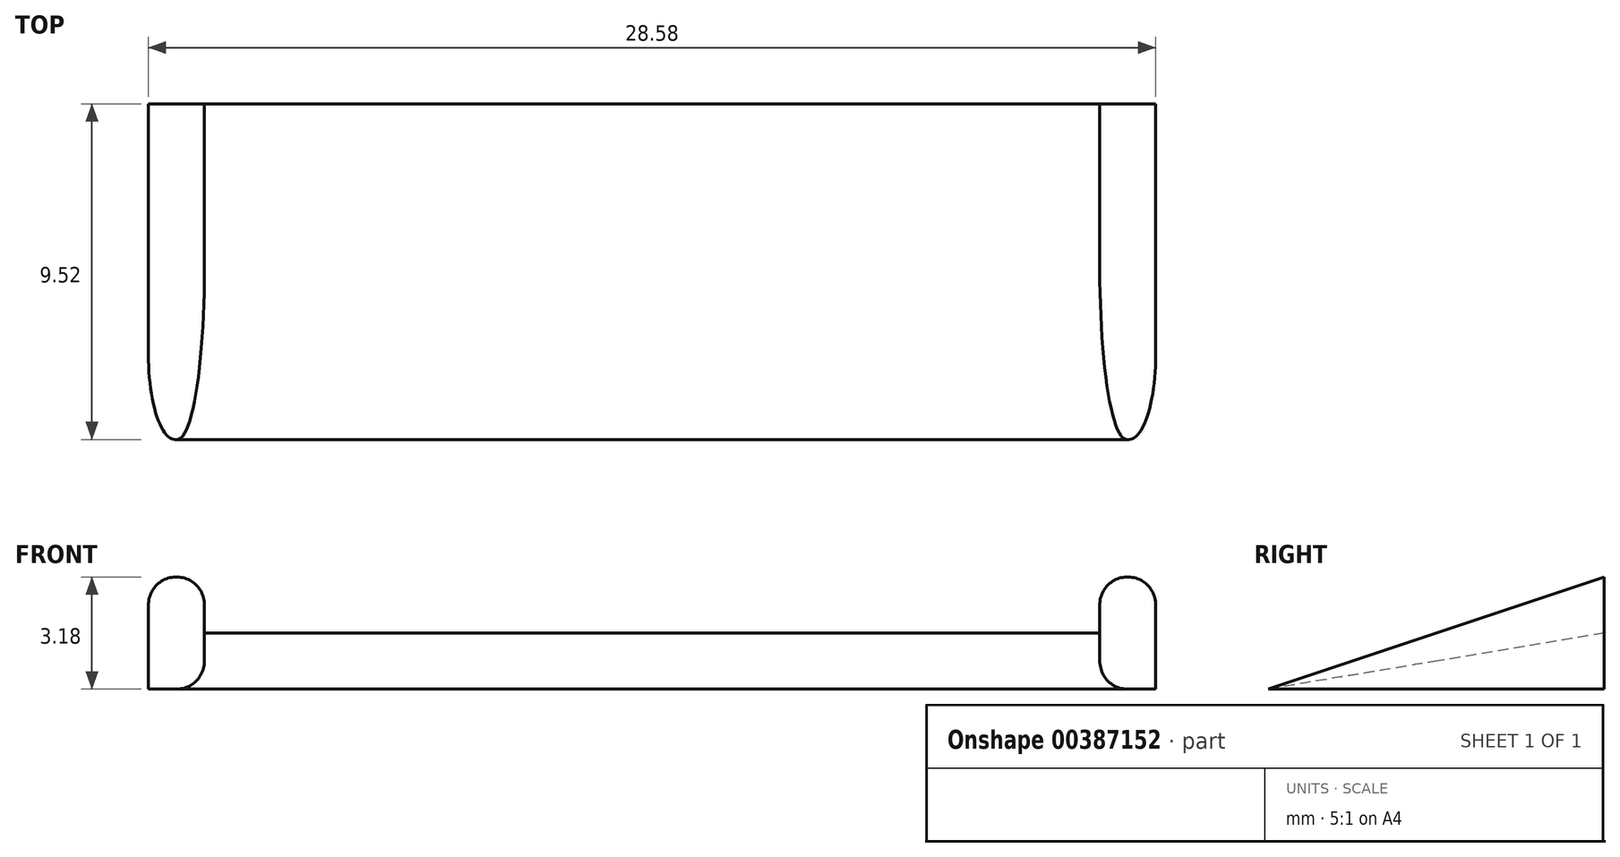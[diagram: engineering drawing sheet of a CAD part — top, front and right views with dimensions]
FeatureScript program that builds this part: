
annotation { "Feature Type Name" : "Feature", "Feature Type Description" : "" }
export const myFeature = defineFeature(function(context is Context, id is Id, definition is map)
    precondition{}
    {
        {
            var Q0;
            Q0=qCreatedBy(makeId("Top.planeOp"),FACE);
            var sketch = newSketch(context, id + "F0", { "sketchPlane" : qUnion([Q0])});
            skLineSegment(sketch, "E0.bottom", {"start": v(-14.29, 4.76) * mm, "end": v(14.29, 4.76) * mm});
            skLineSegment(sketch, "E0.top", {"start": v(-14.29, -4.76) * mm, "end": v(14.29, -4.76) * mm});
            skLineSegment(sketch, "E0.left", {"start": v(-14.29, 4.76) * mm, "end": v(-14.29, -4.76) * mm});
            skLineSegment(sketch, "E0.right", {"start": v(14.29, 4.76) * mm, "end": v(14.29, -4.76) * mm});
            skLineSegment(sketch, "E1", {"start": v(-14.29, 0) * mm, "end": v(14.29, 0) * mm, "construction": true});
            skSolve(sketch);
        }
        {
            var Q0;
            Q0 = qSketchRegion(id + "F0", true);
            extrude(context, id + "F1", {"entities" : qUnion([Q0]), "depth" : 1.59 * mm});
        }
        {
            var Q0;
            Q0=makeQuery(id+"F1.opExtrude","SWEPT_FACE",FACE,{"disambiguationData":[OSD([sQuery(id+"F0.wireOp",EDGE,"E0.left")])]});
            var sketch = newSketch(context, id + "F2", { "sketchPlane" : qUnion([Q0])});
            skLineSegment(sketch, "E2", {"start": v(-4.76, 1.59) * mm, "end": v(4.76, 0) * mm});
            skLineSegment(sketch, "E3", {"start": v(4.76, 0) * mm, "end": v(4.76, 1.59) * mm});
            skLineSegment(sketch, "E4", {"start": v(4.76, 1.59) * mm, "end": v(-4.76, 1.59) * mm});
            skSolve(sketch);
        }
        {
            var Q0;
            Q0 = qSketchRegion(id + "F2", true);
            var Q1;
            Q1=makeQuery(id+"F1.opExtrude","SWEPT_FACE",FACE,{"disambiguationData":[OSD([sQuery(id+"F0.wireOp",EDGE,"E0.right")])]});
            extrude(context, id + "F3", {"entities" : qUnion([Q0]), "operationType" : NewBodyOperationType.REMOVE, "endBound" : BoundingType.UP_TO_SURFACE, "oppositeDirection" : true, "endBoundEntityFace" : qUnion([Q1]), "depth" : 25.4 * mm});
        }
        {
            var Q0;
            Q0=makeQuery(id+"F1.opExtrude","SWEPT_FACE",FACE,{"disambiguationData":[OSD([sQuery(id+"F0.wireOp",EDGE,"E0.left")])]});
            var sketch = newSketch(context, id + "F4", { "sketchPlane" : qUnion([Q0])});
            skLineSegment(sketch, "E5", {"start": v(-4.76, 0) * mm, "end": v(-4.76, 3.18) * mm});
            skLineSegment(sketch, "E6", {"start": v(-4.76, 3.18) * mm, "end": v(4.76, 0) * mm});
            skLineSegment(sketch, "E7", {"start": v(4.76, 0) * mm, "end": v(-4.76, 0) * mm});
            skSolve(sketch);
        }
        {
            var Q0;
            Q0 = qSketchRegion(id + "F4", true);
            extrude(context, id + "F5", {"entities" : qUnion([Q0]), "operationType" : NewBodyOperationType.ADD, "oppositeDirection" : true, "depth" : 1.59 * mm});
        }
        {
            var Q0;
            Q0=makeQuery(id+"F1.opExtrude","SWEPT_FACE",FACE,{"disambiguationData":[OSD([sQuery(id+"F0.wireOp",EDGE,"E0.right")])]});
            var sketch = newSketch(context, id + "F6", { "sketchPlane" : qUnion([Q0])});
            skLineSegment(sketch, "E8", {"start": v(4.76, 0) * mm, "end": v(4.76, 3.18) * mm});
            skLineSegment(sketch, "E9", {"start": v(4.76, 3.18) * mm, "end": v(-4.76, 0) * mm});
            skLineSegment(sketch, "E10", {"start": v(-4.76, 0) * mm, "end": v(4.76, 0) * mm});
            skSolve(sketch);
        }
        {
            var Q0;
            Q0 = qSketchRegion(id + "F6", true);
            extrude(context, id + "F7", {"entities" : qUnion([Q0]), "operationType" : NewBodyOperationType.ADD, "oppositeDirection" : true, "depth" : 1.59 * mm});
        }
        {
            var Q0;
            Q0=makeQuery(id+"F5.opExtrude","CAP_EDGE",EDGE,{"disambiguationData":[OSD([sQuery(id+"F4.wireOp",EDGE,"E6")])],"isStart":true});
            var Q1;
            Q1=makeQuery(id+"F5.opExtrude","CAP_EDGE",EDGE,{"disambiguationData":[OSD([sQuery(id+"F4.wireOp",EDGE,"E6")])],"isStart":false});
            var Q2;
            Q2=makeQuery(id+"F7.opExtrude","CAP_EDGE",EDGE,{"disambiguationData":[OSD([sQuery(id+"F6.wireOp",EDGE,"E9")])],"isStart":false});
            var Q3;
            Q3=makeQuery(id+"F7.opExtrude","CAP_EDGE",EDGE,{"disambiguationData":[OSD([sQuery(id+"F6.wireOp",EDGE,"E9")])],"isStart":true});
            fillet(context, id + "F8", {"entities" : qUnion([Q0, Q1, Q2, Q3]), "radius" : 0.76 * mm, "tangentPropagation" : true, "allowEdgeOverflow" : false});
        }
    });
